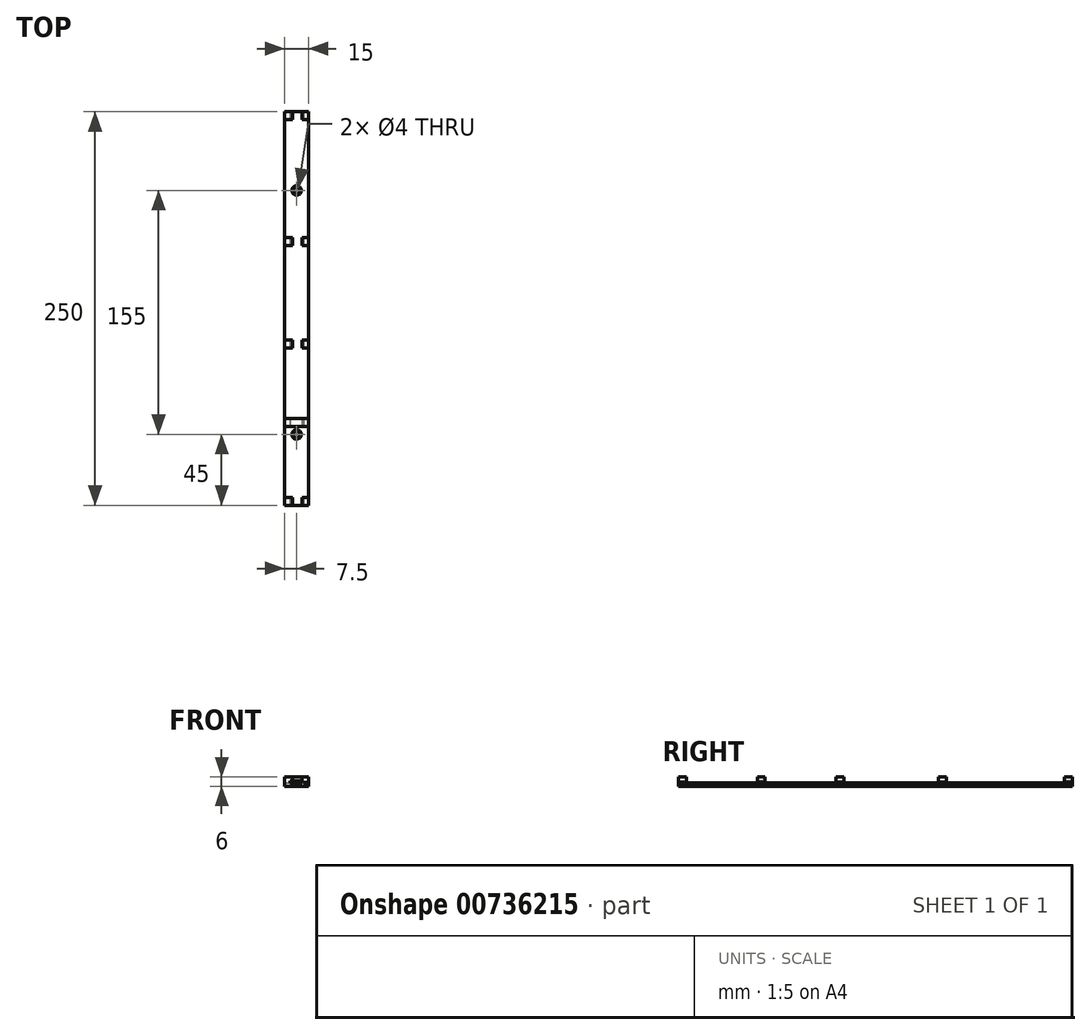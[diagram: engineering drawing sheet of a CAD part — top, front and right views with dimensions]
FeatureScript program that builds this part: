
annotation { "Feature Type Name" : "Feature", "Feature Type Description" : "" }
export const myFeature = defineFeature(function(context is Context, id is Id, definition is map)
    precondition{}
    {
        {
            var Q0;
            Q0=qCreatedBy(makeId("Top.planeOp"),FACE);
            var sketch = newSketch(context, id + "F0", { "sketchPlane" : qUnion([Q0])});
            skLineSegment(sketch, "E0.bottom", {"start": v(7.5, -125) * mm, "end": v(-7.5, -125) * mm});
            skLineSegment(sketch, "E0.top", {"start": v(7.5, 125) * mm, "end": v(-7.5, 125) * mm});
            skLineSegment(sketch, "E0.left", {"start": v(7.5, -125) * mm, "end": v(7.5, 125) * mm});
            skLineSegment(sketch, "E0.right", {"start": v(-7.5, -125) * mm, "end": v(-7.5, 125) * mm});
            skPoint(sketch, "E0.middle", {"position": v(0, 0) * mm});
            skCircle(sketch, "E1", {"center": v(0, 75) * mm, "radius": 2 * mm});
            skCircle(sketch, "E2", {"center": v(0, -80) * mm, "radius": 2 * mm});
            skSolve(sketch);
        }
        {
            var Q0;
            Q0=makeQuery(id+"F0.imprint","IMPRINT",FACE,{"disambiguationData":[TD([[makeQuery(id+"F0.imprint","IMPRINT",EDGE,{"derivedFrom":sQuery(id+"F0.wireOp",EDGE,"E0.bottom")}),-1.0]])]});
            extrude(context, id + "F1", {"entities" : qUnion([Q0]), "depth" : 2 * mm, "offsetDistance" : 25 * mm});
        }
        {
            var Q0;
            Q0=makeQuery(id+"F1.opExtrude","CAP_EDGE",EDGE,{"disambiguationData":[OSD([sQuery(id+"F0.wireOp",EDGE,"E2")])],"isStart":false});
            var Q1;
            Q1=makeQuery(id+"F1.opExtrude","CAP_EDGE",EDGE,{"disambiguationData":[OSD([sQuery(id+"F0.wireOp",EDGE,"E1")])],"isStart":false});
            chamfer(context, id + "F2", {"entities" : qUnion([Q0, Q1]), "width" : 1 * mm, "tangentPropagation" : true});
        }
        {
            var Q0;
            Q0=makeQuery(id+"F1.opExtrude","CAP_FACE",FACE,{"disambiguationData":[OSD([sQuery(id+"F0.wireOp",EDGE,"E0.bottom"),sQuery(id+"F0.wireOp",EDGE,"E0.top"),sQuery(id+"F0.wireOp",EDGE,"E0.left"),sQuery(id+"F0.wireOp",EDGE,"E0.right"),sQuery(id+"F0.wireOp",EDGE,"E1"),sQuery(id+"F0.wireOp",EDGE,"E2")])],"isStart":false});
            var sketch = newSketch(context, id + "F3", { "sketchPlane" : qUnion([Q0])});
            skLineSegment(sketch, "E3.bottom", {"start": v(-7.5, 125) * mm, "end": v(7.5, 125) * mm});
            skLineSegment(sketch, "E3.top", {"start": v(-7.5, 120) * mm, "end": v(7.5, 120) * mm});
            skLineSegment(sketch, "E3.left", {"start": v(-7.5, 125) * mm, "end": v(-7.5, 120) * mm});
            skLineSegment(sketch, "E3.right", {"start": v(7.5, 125) * mm, "end": v(7.5, 120) * mm});
            skLineSegment(sketch, "E4.bottom", {"start": v(-7.5, -20) * mm, "end": v(7.5, -20) * mm});
            skLineSegment(sketch, "E4.top", {"start": v(-7.5, -25) * mm, "end": v(7.5, -25) * mm});
            skLineSegment(sketch, "E4.left", {"start": v(-7.5, -20) * mm, "end": v(-7.5, -25) * mm});
            skLineSegment(sketch, "E4.right", {"start": v(7.5, -20) * mm, "end": v(7.5, -25) * mm});
            skLineSegment(sketch, "E5.bottom", {"start": v(-7.5, -125) * mm, "end": v(7.5, -125) * mm});
            skLineSegment(sketch, "E5.top", {"start": v(-7.5, -120) * mm, "end": v(7.5, -120) * mm});
            skLineSegment(sketch, "E5.left", {"start": v(-7.5, -125) * mm, "end": v(-7.5, -120) * mm});
            skLineSegment(sketch, "E5.right", {"start": v(7.5, -125) * mm, "end": v(7.5, -120) * mm});
            skLineSegment(sketch, "E6.bottom", {"start": v(-7.5, 45) * mm, "end": v(7.5, 45) * mm});
            skLineSegment(sketch, "E6.left", {"start": v(-7.5, 45) * mm, "end": v(-7.5, 40) * mm});
            skLineSegment(sketch, "E7.top", {"start": v(-2.5, 120) * mm, "end": v(3.5, 120) * mm});
            skLineSegment(sketch, "E8.bottom", {"start": v(-2.5, 45) * mm, "end": v(3.5, 45) * mm});
            skLineSegment(sketch, "E8.top", {"start": v(-2.5, 40) * mm, "end": v(3.5, 40) * mm});
            skLineSegment(sketch, "E8.left", {"start": v(-2.5, 45) * mm, "end": v(-2.5, 40) * mm});
            skLineSegment(sketch, "E8.right", {"start": v(3.5, 45) * mm, "end": v(3.5, 40) * mm});
            skLineSegment(sketch, "E9.bottom", {"start": v(-2.5, -20) * mm, "end": v(2.35, -20) * mm});
            skPoint(sketch, "E10.firstSnap0", {"position": v(0, -47.5) * mm});
            skPoint(sketch, "E10.oppositeSnap0", {"position": v(0, -47.5) * mm});
            skLineSegment(sketch, "E11.bottom", {"start": v(-2.5, -120) * mm, "end": v(3.5, -120) * mm});
            skLineSegment(sketch, "E11.top", {"start": v(-2.5, -125) * mm, "end": v(3.5, -125) * mm});
            skLineSegment(sketch, "E11.left", {"start": v(-2.5, -120) * mm, "end": v(-2.5, -125) * mm});
            skLineSegment(sketch, "E11.right", {"start": v(3.5, -120) * mm, "end": v(3.5, -125) * mm});
            skLineSegment(sketch, "E12.bottom", {"start": v(-2.5, -20) * mm, "end": v(3.5, -20) * mm});
            skLineSegment(sketch, "E12.top", {"start": v(-2.5, -25) * mm, "end": v(3.5, -25) * mm});
            skLineSegment(sketch, "E12.left", {"start": v(-2.5, -20) * mm, "end": v(-2.5, -25) * mm});
            skLineSegment(sketch, "E12.right", {"start": v(3.5, -20) * mm, "end": v(3.5, -25) * mm});
            skLineSegment(sketch, "E13", {"start": v(-2.5, 120) * mm, "end": v(-2.5, 125) * mm});
            skLineSegment(sketch, "E14", {"start": v(3.5, 120) * mm, "end": v(3.5, 125) * mm});
            skLineSegment(sketch, "E15", {"start": v(-7.5, 40) * mm, "end": v(-2.5, 40) * mm});
            skLineSegment(sketch, "E16", {"start": v(3.5, 40) * mm, "end": v(7.5, 40) * mm});
            skLineSegment(sketch, "E17", {"start": v(7.5, 45) * mm, "end": v(7.5, 40) * mm});
            skLineSegment(sketch, "E18", {"start": v(-7.5, -70) * mm, "end": v(7.5, -70) * mm});
            skLineSegment(sketch, "E19", {"start": v(7.5, -70) * mm, "end": v(7.5, -75) * mm});
            skLineSegment(sketch, "E20", {"start": v(7.5, -75) * mm, "end": v(-7.5, -75) * mm});
            skLineSegment(sketch, "E21", {"start": v(-7.5, -75) * mm, "end": v(-7.5, -70) * mm});
            skLineSegment(sketch, "E22", {"start": v(-2.5, -75) * mm, "end": v(-2.5, -70) * mm});
            skLineSegment(sketch, "E23", {"start": v(3.5, -75) * mm, "end": v(3.5, -70) * mm});
            skSolve(sketch);
        }
        {
            var Q0;
            Q0=makeQuery(id+"F3.imprint","IMPRINT",FACE,{"disambiguationData":[TD([[makeQuery(id+"F3.imprint","IMPRINT",EDGE,{"derivedFrom":sQuery(id+"F3.wireOp",EDGE,"E7.top")}),1.0]])]});
            var Q1;
            {var subQ0=sQuery(id+"F3.wireOp",EDGE,"E4.left");Q1=makeQuery(id+"F3.imprint","IMPRINT",FACE,{"disambiguationData":[TD([[makeQuery(id+"F3.imprint","IMPRINT",EDGE,{"derivedFrom":subQ0}),-1.0]])]});}
            var Q2;
            {var subQ0=sQuery(id+"F3.wireOp",EDGE,"E4.right");Q2=makeQuery(id+"F3.imprint","IMPRINT",FACE,{"disambiguationData":[TD([[makeQuery(id+"F3.imprint","IMPRINT",EDGE,{"derivedFrom":subQ0}),1.0]])]});}
            var Q3;
            {var subQ0=sQuery(id+"F3.wireOp",EDGE,"E6.left");Q3=makeQuery(id+"F3.imprint","IMPRINT",FACE,{"disambiguationData":[TD([[makeQuery(id+"F3.imprint","IMPRINT",EDGE,{"derivedFrom":subQ0}),-1.0]])]});}
            var Q4;
            {var subQ2=sQuery(id+"F3.wireOp",EDGE,"E8.right");Q4=makeQuery(id+"F3.imprint","IMPRINT",FACE,{"disambiguationData":[TD([[makeQuery(id+"F3.imprint","IMPRINT",EDGE,{"derivedFrom":subQ2}),1.0]])]});}
            var Q5;
            Q5=makeQuery(id+"F3.imprint","IMPRINT",FACE,{"disambiguationData":[TD([[makeQuery(id+"F3.imprint","IMPRINT",EDGE,{"derivedFrom":sQuery(id+"F3.wireOp",EDGE,"E11.bottom")}),-1.0]])]});
            var Q6;
            {var subQ0=sQuery(id+"F3.wireOp",EDGE,"E21");Q6=makeQuery(id+"F3.imprint","IMPRINT",FACE,{"disambiguationData":[TD([[makeQuery(id+"F3.imprint","IMPRINT",EDGE,{"derivedFrom":subQ0}),-1.0]])]});}
            var Q7;
            {var subQ0=sQuery(id+"F3.wireOp",EDGE,"E19");Q7=makeQuery(id+"F3.imprint","IMPRINT",FACE,{"disambiguationData":[TD([[makeQuery(id+"F3.imprint","IMPRINT",EDGE,{"derivedFrom":subQ0}),1.0]])]});}
            var Q8;
            Q8=makeQuery(id+"F3.imprint","IMPRINT",FACE,{"disambiguationData":[TD([[makeQuery(id+"F3.imprint","IMPRINT",EDGE,{"derivedFrom":sQuery(id+"F3.wireOp",EDGE,"E8.bottom")}),-1.0]])]});
            var Q9;
            {var subQ0=sQuery(id+"F3.wireOp",EDGE,"E3.right");Q9=makeQuery(id+"F3.imprint","IMPRINT",FACE,{"disambiguationData":[TD([[makeQuery(id+"F3.imprint","IMPRINT",EDGE,{"derivedFrom":subQ0}),1.0]])]});}
            var Q10;
            {var subQ0=sQuery(id+"F3.wireOp",EDGE,"E3.left");Q10=makeQuery(id+"F3.imprint","IMPRINT",FACE,{"disambiguationData":[TD([[makeQuery(id+"F3.imprint","IMPRINT",EDGE,{"derivedFrom":subQ0}),-1.0]])]});}
            var Q11;
            {var subQ0=sQuery(id+"F3.wireOp",EDGE,"E5.right");Q11=makeQuery(id+"F3.imprint","IMPRINT",FACE,{"disambiguationData":[TD([[makeQuery(id+"F3.imprint","IMPRINT",EDGE,{"derivedFrom":subQ0}),1.0]])]});}
            var Q12;
            {var subQ0=sQuery(id+"F3.wireOp",EDGE,"E5.left");Q12=makeQuery(id+"F3.imprint","IMPRINT",FACE,{"disambiguationData":[TD([[makeQuery(id+"F3.imprint","IMPRINT",EDGE,{"derivedFrom":subQ0}),-1.0]])]});}
            var Q13;
            Q13=makeQuery(id+"F3.imprint","IMPRINT",FACE,{"disambiguationData":[TD([[makeQuery(id+"F3.imprint","IMPRINT",EDGE,{"derivedFrom":sQuery(id+"F3.wireOp",EDGE,"E7.top")}),1.0]])]});
            var Q14;
            {var subQ0=sQuery(id+"F3.wireOp",EDGE,"E4.left");Q14=makeQuery(id+"F3.imprint","IMPRINT",FACE,{"disambiguationData":[TD([[makeQuery(id+"F3.imprint","IMPRINT",EDGE,{"derivedFrom":subQ0}),-1.0]])]});}
            var Q15;
            {var subQ0=sQuery(id+"F3.wireOp",EDGE,"E4.right");Q15=makeQuery(id+"F3.imprint","IMPRINT",FACE,{"disambiguationData":[TD([[makeQuery(id+"F3.imprint","IMPRINT",EDGE,{"derivedFrom":subQ0}),1.0]])]});}
            var Q16;
            {var subQ0=sQuery(id+"F3.wireOp",EDGE,"E6.left");Q16=makeQuery(id+"F3.imprint","IMPRINT",FACE,{"disambiguationData":[TD([[makeQuery(id+"F3.imprint","IMPRINT",EDGE,{"derivedFrom":subQ0}),-1.0]])]});}
            var Q17;
            {var subQ2=sQuery(id+"F3.wireOp",EDGE,"E8.right");Q17=makeQuery(id+"F3.imprint","IMPRINT",FACE,{"disambiguationData":[TD([[makeQuery(id+"F3.imprint","IMPRINT",EDGE,{"derivedFrom":subQ2}),1.0]])]});}
            var Q18;
            {var subQ0=sQuery(id+"F3.wireOp",EDGE,"E21");Q18=makeQuery(id+"F3.imprint","IMPRINT",FACE,{"disambiguationData":[TD([[makeQuery(id+"F3.imprint","IMPRINT",EDGE,{"derivedFrom":subQ0}),-1.0]])]});}
            var Q19;
            {var subQ0=sQuery(id+"F3.wireOp",EDGE,"E19");Q19=makeQuery(id+"F3.imprint","IMPRINT",FACE,{"disambiguationData":[TD([[makeQuery(id+"F3.imprint","IMPRINT",EDGE,{"derivedFrom":subQ0}),1.0]])]});}
            var Q20;
            Q20=makeQuery(id+"F3.imprint","IMPRINT",FACE,{"disambiguationData":[TD([[makeQuery(id+"F3.imprint","IMPRINT",EDGE,{"derivedFrom":sQuery(id+"F3.wireOp",EDGE,"E8.bottom")}),-1.0]])]});
            var Q21;
            {var subQ0=sQuery(id+"F3.wireOp",EDGE,"E22");Q21=makeQuery(id+"F3.imprint","IMPRINT",FACE,{"disambiguationData":[TD([[makeQuery(id+"F3.imprint","IMPRINT",EDGE,{"derivedFrom":subQ0}),-1.0]])]});}
            var Q22;
            {var subQ0=sQuery(id+"F3.wireOp",EDGE,"E3.right");Q22=makeQuery(id+"F3.imprint","IMPRINT",FACE,{"disambiguationData":[TD([[makeQuery(id+"F3.imprint","IMPRINT",EDGE,{"derivedFrom":subQ0}),1.0]])]});}
            var Q23;
            {var subQ0=sQuery(id+"F3.wireOp",EDGE,"E3.left");Q23=makeQuery(id+"F3.imprint","IMPRINT",FACE,{"disambiguationData":[TD([[makeQuery(id+"F3.imprint","IMPRINT",EDGE,{"derivedFrom":subQ0}),-1.0]])]});}
            var Q24;
            {var subQ0=sQuery(id+"F3.wireOp",EDGE,"E5.right");Q24=makeQuery(id+"F3.imprint","IMPRINT",FACE,{"disambiguationData":[TD([[makeQuery(id+"F3.imprint","IMPRINT",EDGE,{"derivedFrom":subQ0}),1.0]])]});}
            var Q25;
            {var subQ0=sQuery(id+"F3.wireOp",EDGE,"E5.left");Q25=makeQuery(id+"F3.imprint","IMPRINT",FACE,{"disambiguationData":[TD([[makeQuery(id+"F3.imprint","IMPRINT",EDGE,{"derivedFrom":subQ0}),-1.0]])]});}
            var Q26;
            Q26=makeQuery(id+"F3.imprint","IMPRINT",FACE,{"disambiguationData":[TD([[makeQuery(id+"F3.imprint","IMPRINT",EDGE,{"derivedFrom":sQuery(id+"F3.wireOp",EDGE,"E7.top")}),1.0]])]});
            var Q27;
            {var subQ0=sQuery(id+"F3.wireOp",EDGE,"E4.left");Q27=makeQuery(id+"F3.imprint","IMPRINT",FACE,{"disambiguationData":[TD([[makeQuery(id+"F3.imprint","IMPRINT",EDGE,{"derivedFrom":subQ0}),-1.0]])]});}
            var Q28;
            {var subQ0=sQuery(id+"F3.wireOp",EDGE,"E4.right");Q28=makeQuery(id+"F3.imprint","IMPRINT",FACE,{"disambiguationData":[TD([[makeQuery(id+"F3.imprint","IMPRINT",EDGE,{"derivedFrom":subQ0}),1.0]])]});}
            var Q29;
            {var subQ0=sQuery(id+"F3.wireOp",EDGE,"E6.left");Q29=makeQuery(id+"F3.imprint","IMPRINT",FACE,{"disambiguationData":[TD([[makeQuery(id+"F3.imprint","IMPRINT",EDGE,{"derivedFrom":subQ0}),-1.0]])]});}
            var Q30;
            {var subQ2=sQuery(id+"F3.wireOp",EDGE,"E8.right");Q30=makeQuery(id+"F3.imprint","IMPRINT",FACE,{"disambiguationData":[TD([[makeQuery(id+"F3.imprint","IMPRINT",EDGE,{"derivedFrom":subQ2}),1.0]])]});}
            var Q31;
            {var subQ0=sQuery(id+"F3.wireOp",EDGE,"E21");Q31=makeQuery(id+"F3.imprint","IMPRINT",FACE,{"disambiguationData":[TD([[makeQuery(id+"F3.imprint","IMPRINT",EDGE,{"derivedFrom":subQ0}),-1.0]])]});}
            var Q32;
            {var subQ0=sQuery(id+"F3.wireOp",EDGE,"E19");Q32=makeQuery(id+"F3.imprint","IMPRINT",FACE,{"disambiguationData":[TD([[makeQuery(id+"F3.imprint","IMPRINT",EDGE,{"derivedFrom":subQ0}),1.0]])]});}
            var Q33;
            Q33=makeQuery(id+"F3.imprint","IMPRINT",FACE,{"disambiguationData":[TD([[makeQuery(id+"F3.imprint","IMPRINT",EDGE,{"derivedFrom":sQuery(id+"F3.wireOp",EDGE,"E12.top")}),1.0]])]});
            var Q34;
            {var subQ0=sQuery(id+"F3.wireOp",EDGE,"E22");Q34=makeQuery(id+"F3.imprint","IMPRINT",FACE,{"disambiguationData":[TD([[makeQuery(id+"F3.imprint","IMPRINT",EDGE,{"derivedFrom":subQ0}),-1.0]])]});}
            var Q35;
            {var subQ0=sQuery(id+"F3.wireOp",EDGE,"E3.right");Q35=makeQuery(id+"F3.imprint","IMPRINT",FACE,{"disambiguationData":[TD([[makeQuery(id+"F3.imprint","IMPRINT",EDGE,{"derivedFrom":subQ0}),1.0]])]});}
            var Q36;
            {var subQ0=sQuery(id+"F3.wireOp",EDGE,"E3.left");Q36=makeQuery(id+"F3.imprint","IMPRINT",FACE,{"disambiguationData":[TD([[makeQuery(id+"F3.imprint","IMPRINT",EDGE,{"derivedFrom":subQ0}),-1.0]])]});}
            var Q37;
            {var subQ0=sQuery(id+"F3.wireOp",EDGE,"E5.right");Q37=makeQuery(id+"F3.imprint","IMPRINT",FACE,{"disambiguationData":[TD([[makeQuery(id+"F3.imprint","IMPRINT",EDGE,{"derivedFrom":subQ0}),1.0]])]});}
            var Q38;
            {var subQ0=sQuery(id+"F3.wireOp",EDGE,"E5.left");Q38=makeQuery(id+"F3.imprint","IMPRINT",FACE,{"disambiguationData":[TD([[makeQuery(id+"F3.imprint","IMPRINT",EDGE,{"derivedFrom":subQ0}),-1.0]])]});}
            var Q39;
            {var subQ0=sQuery(id+"F3.wireOp",EDGE,"E4.left");Q39=makeQuery(id+"F3.imprint","IMPRINT",FACE,{"disambiguationData":[TD([[makeQuery(id+"F3.imprint","IMPRINT",EDGE,{"derivedFrom":subQ0}),-1.0]])]});}
            var Q40;
            {var subQ0=sQuery(id+"F3.wireOp",EDGE,"E4.right");Q40=makeQuery(id+"F3.imprint","IMPRINT",FACE,{"disambiguationData":[TD([[makeQuery(id+"F3.imprint","IMPRINT",EDGE,{"derivedFrom":subQ0}),1.0]])]});}
            var Q41;
            {var subQ0=sQuery(id+"F3.wireOp",EDGE,"E6.left");Q41=makeQuery(id+"F3.imprint","IMPRINT",FACE,{"disambiguationData":[TD([[makeQuery(id+"F3.imprint","IMPRINT",EDGE,{"derivedFrom":subQ0}),-1.0]])]});}
            var Q42;
            {var subQ2=sQuery(id+"F3.wireOp",EDGE,"E8.right");Q42=makeQuery(id+"F3.imprint","IMPRINT",FACE,{"disambiguationData":[TD([[makeQuery(id+"F3.imprint","IMPRINT",EDGE,{"derivedFrom":subQ2}),1.0]])]});}
            var Q43;
            Q43=makeQuery(id+"F3.imprint","IMPRINT",FACE,{"disambiguationData":[TD([[makeQuery(id+"F3.imprint","IMPRINT",EDGE,{"derivedFrom":sQuery(id+"F3.wireOp",EDGE,"E11.bottom")}),-1.0]])]});
            var Q44;
            {var subQ0=sQuery(id+"F3.wireOp",EDGE,"E21");Q44=makeQuery(id+"F3.imprint","IMPRINT",FACE,{"disambiguationData":[TD([[makeQuery(id+"F3.imprint","IMPRINT",EDGE,{"derivedFrom":subQ0}),-1.0]])]});}
            var Q45;
            {var subQ0=sQuery(id+"F3.wireOp",EDGE,"E19");Q45=makeQuery(id+"F3.imprint","IMPRINT",FACE,{"disambiguationData":[TD([[makeQuery(id+"F3.imprint","IMPRINT",EDGE,{"derivedFrom":subQ0}),1.0]])]});}
            var Q46;
            Q46=makeQuery(id+"F3.imprint","IMPRINT",FACE,{"disambiguationData":[TD([[makeQuery(id+"F3.imprint","IMPRINT",EDGE,{"derivedFrom":sQuery(id+"F3.wireOp",EDGE,"E12.top")}),1.0]])]});
            var Q47;
            {var subQ0=sQuery(id+"F3.wireOp",EDGE,"E22");Q47=makeQuery(id+"F3.imprint","IMPRINT",FACE,{"disambiguationData":[TD([[makeQuery(id+"F3.imprint","IMPRINT",EDGE,{"derivedFrom":subQ0}),-1.0]])]});}
            var Q48;
            {var subQ0=sQuery(id+"F3.wireOp",EDGE,"E3.right");Q48=makeQuery(id+"F3.imprint","IMPRINT",FACE,{"disambiguationData":[TD([[makeQuery(id+"F3.imprint","IMPRINT",EDGE,{"derivedFrom":subQ0}),1.0]])]});}
            var Q49;
            {var subQ0=sQuery(id+"F3.wireOp",EDGE,"E3.left");Q49=makeQuery(id+"F3.imprint","IMPRINT",FACE,{"disambiguationData":[TD([[makeQuery(id+"F3.imprint","IMPRINT",EDGE,{"derivedFrom":subQ0}),-1.0]])]});}
            var Q50;
            {var subQ0=sQuery(id+"F3.wireOp",EDGE,"E5.right");Q50=makeQuery(id+"F3.imprint","IMPRINT",FACE,{"disambiguationData":[TD([[makeQuery(id+"F3.imprint","IMPRINT",EDGE,{"derivedFrom":subQ0}),1.0]])]});}
            var Q51;
            {var subQ0=sQuery(id+"F3.wireOp",EDGE,"E5.left");Q51=makeQuery(id+"F3.imprint","IMPRINT",FACE,{"disambiguationData":[TD([[makeQuery(id+"F3.imprint","IMPRINT",EDGE,{"derivedFrom":subQ0}),-1.0]])]});}
            var Q52;
            {var subQ0=sQuery(id+"F3.wireOp",EDGE,"E4.left");Q52=makeQuery(id+"F3.imprint","IMPRINT",FACE,{"disambiguationData":[TD([[makeQuery(id+"F3.imprint","IMPRINT",EDGE,{"derivedFrom":subQ0}),-1.0]])]});}
            var Q53;
            {var subQ0=sQuery(id+"F3.wireOp",EDGE,"E4.right");Q53=makeQuery(id+"F3.imprint","IMPRINT",FACE,{"disambiguationData":[TD([[makeQuery(id+"F3.imprint","IMPRINT",EDGE,{"derivedFrom":subQ0}),1.0]])]});}
            var Q54;
            {var subQ0=sQuery(id+"F3.wireOp",EDGE,"E6.left");Q54=makeQuery(id+"F3.imprint","IMPRINT",FACE,{"disambiguationData":[TD([[makeQuery(id+"F3.imprint","IMPRINT",EDGE,{"derivedFrom":subQ0}),-1.0]])]});}
            var Q55;
            {var subQ2=sQuery(id+"F3.wireOp",EDGE,"E8.right");Q55=makeQuery(id+"F3.imprint","IMPRINT",FACE,{"disambiguationData":[TD([[makeQuery(id+"F3.imprint","IMPRINT",EDGE,{"derivedFrom":subQ2}),1.0]])]});}
            var Q56;
            Q56=makeQuery(id+"F3.imprint","IMPRINT",FACE,{"disambiguationData":[TD([[makeQuery(id+"F3.imprint","IMPRINT",EDGE,{"derivedFrom":sQuery(id+"F3.wireOp",EDGE,"E11.bottom")}),-1.0]])]});
            var Q57;
            {var subQ0=sQuery(id+"F3.wireOp",EDGE,"E21");Q57=makeQuery(id+"F3.imprint","IMPRINT",FACE,{"disambiguationData":[TD([[makeQuery(id+"F3.imprint","IMPRINT",EDGE,{"derivedFrom":subQ0}),-1.0]])]});}
            var Q58;
            {var subQ0=sQuery(id+"F3.wireOp",EDGE,"E19");Q58=makeQuery(id+"F3.imprint","IMPRINT",FACE,{"disambiguationData":[TD([[makeQuery(id+"F3.imprint","IMPRINT",EDGE,{"derivedFrom":subQ0}),1.0]])]});}
            var Q59;
            Q59=makeQuery(id+"F3.imprint","IMPRINT",FACE,{"disambiguationData":[TD([[makeQuery(id+"F3.imprint","IMPRINT",EDGE,{"derivedFrom":sQuery(id+"F3.wireOp",EDGE,"E8.bottom")}),-1.0]])]});
            var Q60;
            Q60=makeQuery(id+"F3.imprint","IMPRINT",FACE,{"disambiguationData":[TD([[makeQuery(id+"F3.imprint","IMPRINT",EDGE,{"derivedFrom":sQuery(id+"F3.wireOp",EDGE,"E12.top")}),1.0]])]});
            var Q61;
            {var subQ0=sQuery(id+"F3.wireOp",EDGE,"E22");Q61=makeQuery(id+"F3.imprint","IMPRINT",FACE,{"disambiguationData":[TD([[makeQuery(id+"F3.imprint","IMPRINT",EDGE,{"derivedFrom":subQ0}),-1.0]])]});}
            extrude(context, id + "F4", {"entities" : qUnion([Q0, Q1, Q2, Q3, Q4, Q5, Q6, Q7, Q8, Q9, Q10, Q11, Q12, Q13, Q14, Q15, Q16, Q17, Q18, Q19, Q20, Q21, Q22, Q23, Q24, Q25, Q26, Q27, Q28, Q29, Q30, Q31, Q32, Q33, Q34, Q35, Q36, Q37, Q38, Q39, Q40, Q41, Q42, Q43, Q44, Q45, Q46, Q47, Q48, Q49, Q50, Q51, Q52, Q53, Q54, Q55, Q56, Q57, Q58, Q59, Q60, Q61]), "operationType" : NewBodyOperationType.ADD, "depth" : 4 * mm, "offsetDistance" : 25 * mm});
        }
        {
            var Q0;
            Q0=makeQuery(id+"F4.boolean.opBoolean","MERGE",FACE,{"derivedFrom":[makeQuery(id+"F1.opExtrude","SWEPT_FACE",FACE,{"disambiguationData":[OSD([sQuery(id+"F0.wireOp",EDGE,"E0.bottom")])]}),makeQuery(id+"F4.opExtrude","SWEPT_FACE",FACE,{"disambiguationData":[OSD([sQuery(id+"F3.wireOp",EDGE,"E5.bottom"),sQuery(id+"F3.wireOp",EDGE,"E11.top")])]})]});
            var sketch = newSketch(context, id + "F5", { "sketchPlane" : qUnion([Q0])});
            skLineSegment(sketch, "E24.bottom", {"start": v(-4, 2) * mm, "end": v(4.5, 2) * mm});
            skLineSegment(sketch, "E24.top", {"start": v(-4, 3.5) * mm, "end": v(4.5, 3.5) * mm});
            skLineSegment(sketch, "E24.left", {"start": v(-4, 2) * mm, "end": v(-4, 3.5) * mm});
            skLineSegment(sketch, "E24.right", {"start": v(4.5, 2) * mm, "end": v(4.5, 3.5) * mm});
            skLineSegment(sketch, "E25.bottom", {"start": v(4.5, 2) * mm, "end": v(7.5, 2) * mm});
            skLineSegment(sketch, "E25.top", {"start": v(4.5, 2.5) * mm, "end": v(7.5, 2.5) * mm});
            skLineSegment(sketch, "E25.left", {"start": v(4.5, 2) * mm, "end": v(4.5, 2.5) * mm});
            skLineSegment(sketch, "E25.right", {"start": v(7.5, 2) * mm, "end": v(7.5, 2.5) * mm});
            skSolve(sketch);
        }
        {
            var Q0;
            Q0=makeQuery(id+"F5.imprint","IMPRINT",FACE,{"disambiguationData":[TD([[makeQuery(id+"F5.imprint","IMPRINT",EDGE,{"derivedFrom":sQuery(id+"F5.wireOp",EDGE,"E24.bottom")}),1.0]])]});
            var Q1;
            Q1=makeQuery(id+"F5.imprint","IMPRINT",FACE,{"disambiguationData":[TD([[makeQuery(id+"F5.imprint","IMPRINT",EDGE,{"derivedFrom":sQuery(id+"F5.wireOp",EDGE,"E25.bottom")}),1.0]])]});
            extrude(context, id + "F6", {"entities" : qUnion([Q0, Q1]), "operationType" : NewBodyOperationType.REMOVE, "oppositeDirection" : true, "depth" : 250 * mm, "offsetDistance" : 25 * mm});
        }
    });
